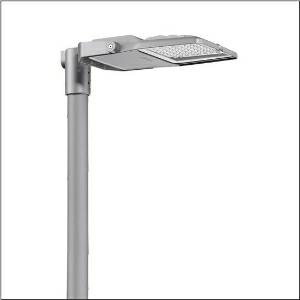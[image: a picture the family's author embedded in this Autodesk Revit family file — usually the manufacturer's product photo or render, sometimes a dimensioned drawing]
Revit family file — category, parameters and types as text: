
# Revit family: floodlight_fl_21_iq_mini___pl61_5xa7771c2c3a_2691
name_source: partatom
category: Lighting Fixtures
units: mm (PartAtom-declared; Revit-internal decimal feet)

## family parameters
Cut with Voids When Loaded = No
Host = Face
Light Source = No
Part Type = Normal
Room Calculation Point = No
Round Connector Dimension = Use Diameter
Shared = No

## types (1)
- --- (1 x LED, 11980 lm, 87.2 W, 3000K)
    Apparent Load = 87 VA
    CIE Flux Codes = 33 65 98 100 100
    Color Rendering = 70
    Color Temperature = 3000K
    Default Elevation = 1800 mm
    Description = Floodlight FL 21 iQ mini, floodlight, primary light control with lens, of PMMA, primary optical cover: protective disc, of toughened safety glass, transparent, light distribution: PL61, light emission: direct distribution, installation type: surface-mounted, LED, High Power LED, rated luminous flux: 11.980lm, luminous efficacy: 137lm/W, light colour: 730, colour temperature: 3000K, control gear: iQ Comfort/DALI, control: Auto-Match, Temp-Guard, Lumen-Switch, Night-Set, Smart-Wire, Light-Fading, Desk-Remote (wireless, voltage-free reading and setting of iQ features in the workshop via application-optimized NFC function/RFID function), optimised constant luminous flux control (CLO 2.0), with terminal, 6-pole, mains connection: 220..240V, AC, 50/60Hz, start of lifetime: 87W, end of service life: 92W, reduction: 40W, luminaire housing, of diecast aluminium, powder-coated, Siteco® metallic grey (DB 702S), corrosivity category C5 mid according to DIN EN ISO 12944, suitable for swimming pools, chlorine-resistant, sealing non-destructively replaceable, please order mast flange separately, mast bracket, of steel, galvanised, powder-coated, Siteco® metallic grey (DB 702S), protection rating (complete): IP66, insulation class (complete): insulation class II (safety insulation), certification: CE, ENEC, VDE, protection symbol: D, impact resistance: IK08, permissible operating ambient temperature: -40..+40°C, permissible operating ambient temperature for outdoor applications: -40..+50°C, standard: DIN EN 12944, LABS conformity tested according to VDMA 24364:2018-05, packaging unit: 1 piece

Light Distribution: PL61
    Height = 70 mm
    Lamp = 1 x LED
    Lamp Light Flux = 11980 lm
    Lamp Power = 87.2 W
    Lamp count = 1
    Length = 485 mm
    Luminous efficacy = 137 lm/W
    Manufacturer = Siteco
    ModVariant = No
    Model = 5XA7771C2C3A
    Number of Poles = 1
    OnlyDefault = Yes
    Power Factor = 1
    Product Name = Floodlight FL 21 iQ mini | PL61
    Product group = floodlight | pylon annexe
    ProductGroupID = 6201
    Protection Class = Protection class II
    Protection Degree = IP 66
    RLX_Detail_Level = 1
    RLX_Emergency_Light_Flux = 0 lm
    RLX_Emergency_Type = 0
    RLX_Emergency_Type_DB = No
    RlxData = <blob elided: 101405 chars, md5=23080994>
    Socket = socket
    Standby Power = 0 W
    System Light Flux = 11980 lm
    System Power = 87 W
    Type Comments = factory setting: luminous flux: 100 % | dim-lin: 254 | 456 mA
    Type Image = l_1007125.jpg
    URL = http://relux.com
    VarID = @adj_194769
    Voltage = 0 V
    Weight = 0.00 kg
    Width = 337 mm

## geometry (parser evidence)
native form markers: Blend x4, Sweep x11
no freeform markers — native parametric forms only
